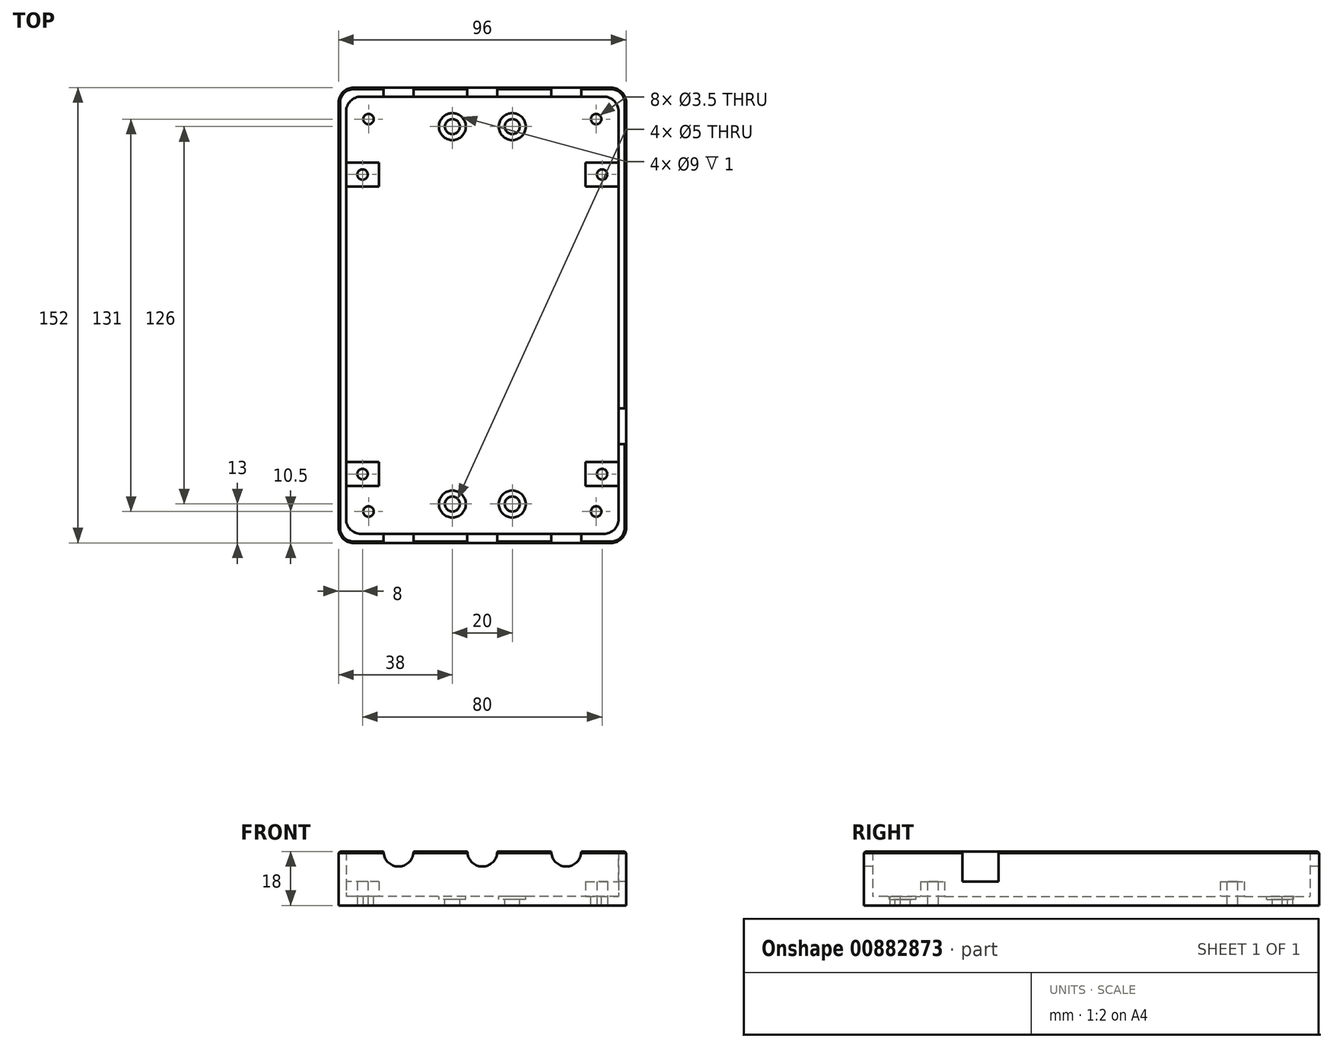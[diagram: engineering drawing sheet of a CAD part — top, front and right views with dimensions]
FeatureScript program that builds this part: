
annotation { "Feature Type Name" : "Feature", "Feature Type Description" : "" }
export const myFeature = defineFeature(function(context is Context, id is Id, definition is map)
    precondition{}
    {
        {
            var Q0;
            Q0=qCreatedBy(makeId("Top.planeOp"),FACE);
            var sketch = newSketch(context, id + "F0", { "sketchPlane" : qUnion([Q0])});
            skLineSegment(sketch, "E0.bottom", {"start": v(48, -76) * mm, "end": v(-48, -76) * mm});
            skLineSegment(sketch, "E0.top", {"start": v(48, 76) * mm, "end": v(-48, 76) * mm});
            skLineSegment(sketch, "E0.left", {"start": v(48, -76) * mm, "end": v(48, 76) * mm});
            skLineSegment(sketch, "E0.right", {"start": v(-48, -76) * mm, "end": v(-48, 76) * mm});
            skPoint(sketch, "E0.middle", {"position": v(0, 0) * mm});
            skSolve(sketch);
        }
        {
            var Q0;
            Q0 = qSketchRegion(id + "F0", true);
            extrude(context, id + "F1", {"entities" : qUnion([Q0]), "depth" : 3 * mm, "offsetDistance" : 25 * mm});
        }
        {
            var Q0;
            Q0=makeQuery(id+"F1.opExtrude","CAP_FACE",FACE,{"disambiguationData":[OSD([sQuery(id+"F0.wireOp",EDGE,"E0.bottom"),sQuery(id+"F0.wireOp",EDGE,"E0.top"),sQuery(id+"F0.wireOp",EDGE,"E0.left"),sQuery(id+"F0.wireOp",EDGE,"E0.right")])],"isStart":false});
            var sketch = newSketch(context, id + "F2", { "sketchPlane" : qUnion([Q0])});
            skLineSegment(sketch, "E1.bottom", {"start": v(48, -76) * mm, "end": v(-48, -76) * mm});
            skLineSegment(sketch, "E1.top", {"start": v(48, 76) * mm, "end": v(-48, 76) * mm});
            skLineSegment(sketch, "E1.left", {"start": v(48, -76) * mm, "end": v(48, 76) * mm});
            skLineSegment(sketch, "E1.right", {"start": v(-48, -76) * mm, "end": v(-48, 76) * mm});
            skPoint(sketch, "E1.middle", {"position": v(0, 0) * mm});
            skLineSegment(sketch, "E2.bottom", {"start": v(45.5, -73) * mm, "end": v(-45.5, -73) * mm});
            skLineSegment(sketch, "E2.top", {"start": v(45.5, 73) * mm, "end": v(-45.5, 73) * mm});
            skLineSegment(sketch, "E2.left", {"start": v(45.5, -73) * mm, "end": v(45.5, 73) * mm});
            skLineSegment(sketch, "E2.right", {"start": v(-45.5, -73) * mm, "end": v(-45.5, 73) * mm});
            skSolve(sketch);
        }
        {
            var Q0;
            Q0 = qSketchRegion(id + "F2", true);
            extrude(context, id + "F3", {"entities" : qUnion([Q0]), "operationType" : NewBodyOperationType.ADD, "depth" : 15 * mm, "offsetDistance" : 25 * mm});
        }
        {
            var Q0;
            Q0=makeQuery(id+"F1.opExtrude","CAP_FACE",FACE,{"disambiguationData":[OSD([sQuery(id+"F0.wireOp",EDGE,"E0.bottom"),sQuery(id+"F0.wireOp",EDGE,"E0.top"),sQuery(id+"F0.wireOp",EDGE,"E0.left"),sQuery(id+"F0.wireOp",EDGE,"E0.right")])],"isStart":false});
            var sketch = newSketch(context, id + "F4", { "sketchPlane" : qUnion([Q0])});
            skCircle(sketch, "E3", {"center": v(-38, 65.5) * mm, "radius": 1.75 * mm});
            skCircle(sketch, "E4.MirrorC", {"center": v(38, 65.5) * mm, "radius": 1.75 * mm});
            skCircle(sketch, "E5.MirrorC", {"center": v(-38, -65.5) * mm, "radius": 1.75 * mm});
            skCircle(sketch, "E6.MirrorC", {"center": v(38, -65.5) * mm, "radius": 1.75 * mm});
            skSolve(sketch);
        }
        {
            var Q0;
            Q0 = qSketchRegion(id + "F4", true);
            extrude(context, id + "F5", {"entities" : qUnion([Q0]), "operationType" : NewBodyOperationType.REMOVE, "endBound" : BoundingType.UP_TO_NEXT, "oppositeDirection" : true, "depth" : 25 * mm, "offsetDistance" : 25 * mm});
        }
        {
            var Q0;
            Q0=makeQuery(id+"F3.boolean.opBoolean","MERGE",EDGE,{"derivedFrom":[makeQuery(id+"F1.opExtrude","SWEPT_EDGE",EDGE,{"disambiguationData":[OSD([sQuery(id+"F0.wireOp",EDGE,"E0.bottom"),sQuery(id+"F0.wireOp",EDGE,"E0.right")])]}),makeQuery(id+"F3.opExtrude","SWEPT_EDGE",EDGE,{"disambiguationData":[OSD([sQuery(id+"F2.wireOp",EDGE,"E1.bottom"),sQuery(id+"F2.wireOp",EDGE,"E1.right")])]})]});
            var Q1;
            Q1=makeQuery(id+"F3.boolean.opBoolean","MERGE",EDGE,{"derivedFrom":[makeQuery(id+"F1.opExtrude","SWEPT_EDGE",EDGE,{"disambiguationData":[OSD([sQuery(id+"F0.wireOp",EDGE,"E0.bottom"),sQuery(id+"F0.wireOp",EDGE,"E0.left")])]}),makeQuery(id+"F3.opExtrude","SWEPT_EDGE",EDGE,{"disambiguationData":[OSD([sQuery(id+"F2.wireOp",EDGE,"E1.bottom"),sQuery(id+"F2.wireOp",EDGE,"E1.left")])]})]});
            var Q2;
            Q2=makeQuery(id+"F3.opExtrude","SWEPT_EDGE",EDGE,{"disambiguationData":[OSD([sQuery(id+"F2.wireOp",EDGE,"E2.bottom"),sQuery(id+"F2.wireOp",EDGE,"E2.left")])]});
            var Q3;
            Q3=makeQuery(id+"F3.opExtrude","SWEPT_EDGE",EDGE,{"disambiguationData":[OSD([sQuery(id+"F2.wireOp",EDGE,"E2.bottom"),sQuery(id+"F2.wireOp",EDGE,"E2.right")])]});
            var Q4;
            Q4=makeQuery(id+"F3.boolean.opBoolean","MERGE",EDGE,{"derivedFrom":[makeQuery(id+"F1.opExtrude","SWEPT_EDGE",EDGE,{"disambiguationData":[OSD([sQuery(id+"F0.wireOp",EDGE,"E0.top"),sQuery(id+"F0.wireOp",EDGE,"E0.right")])]}),makeQuery(id+"F3.opExtrude","SWEPT_EDGE",EDGE,{"disambiguationData":[OSD([sQuery(id+"F2.wireOp",EDGE,"E1.top"),sQuery(id+"F2.wireOp",EDGE,"E1.right")])]})]});
            var Q5;
            Q5=makeQuery(id+"F3.opExtrude","SWEPT_EDGE",EDGE,{"disambiguationData":[OSD([sQuery(id+"F2.wireOp",EDGE,"E2.top"),sQuery(id+"F2.wireOp",EDGE,"E2.right")])]});
            var Q6;
            Q6=makeQuery(id+"F3.boolean.opBoolean","MERGE",EDGE,{"derivedFrom":[makeQuery(id+"F1.opExtrude","SWEPT_EDGE",EDGE,{"disambiguationData":[OSD([sQuery(id+"F0.wireOp",EDGE,"E0.top"),sQuery(id+"F0.wireOp",EDGE,"E0.left")])]}),makeQuery(id+"F3.opExtrude","SWEPT_EDGE",EDGE,{"disambiguationData":[OSD([sQuery(id+"F2.wireOp",EDGE,"E1.top"),sQuery(id+"F2.wireOp",EDGE,"E1.left")])]})]});
            var Q7;
            Q7=makeQuery(id+"F3.opExtrude","SWEPT_EDGE",EDGE,{"disambiguationData":[OSD([sQuery(id+"F2.wireOp",EDGE,"E2.top"),sQuery(id+"F2.wireOp",EDGE,"E2.left")])]});
            fillet(context, id + "F6", {"entities" : qUnion([Q0, Q1, Q2, Q3, Q4, Q5, Q6, Q7]), "radius" : 5 * mm, "tangentPropagation" : true, "allowEdgeOverflow" : false});
        }
        {
            var Q0;
            Q0=makeQuery(id+"F3.boolean.opBoolean","MERGE",FACE,{"derivedFrom":[makeQuery(id+"F1.opExtrude","SWEPT_FACE",FACE,{"disambiguationData":[OSD([sQuery(id+"F0.wireOp",EDGE,"E0.bottom")])]}),makeQuery(id+"F3.opExtrude","SWEPT_FACE",FACE,{"disambiguationData":[OSD([sQuery(id+"F2.wireOp",EDGE,"E1.bottom")])]})]});
            var sketch = newSketch(context, id + "F7", { "sketchPlane" : qUnion([Q0])});
            skCircle(sketch, "E7", {"center": v(-28, 18) * mm, "radius": 5 * mm});
            skCircle(sketch, "E8", {"center": v(0, 18) * mm, "radius": 5 * mm});
            skCircle(sketch, "E9", {"center": v(28, 18) * mm, "radius": 5 * mm});
            skSolve(sketch);
        }
        {
            var Q0;
            Q0 = qSketchRegion(id + "F7", true);
            extrude(context, id + "F8", {"entities" : qUnion([Q0]), "operationType" : NewBodyOperationType.REMOVE, "endBound" : BoundingType.THROUGH_ALL, "oppositeDirection" : true, "depth" : 25 * mm, "offsetDistance" : 25 * mm});
        }
        {
            var Q0;
            Q0=makeQuery(id+"F1.opExtrude","CAP_FACE",FACE,{"disambiguationData":[OSD([sQuery(id+"F0.wireOp",EDGE,"E0.bottom"),sQuery(id+"F0.wireOp",EDGE,"E0.top"),sQuery(id+"F0.wireOp",EDGE,"E0.left"),sQuery(id+"F0.wireOp",EDGE,"E0.right")])],"isStart":false});
            var sketch = newSketch(context, id + "F9", { "sketchPlane" : qUnion([Q0])});
            skLineSegment(sketch, "E10.bottom", {"start": v(-34.5, -49) * mm, "end": v(-45.5, -49) * mm});
            skLineSegment(sketch, "E10.top", {"start": v(-34.5, -57) * mm, "end": v(-45.5, -57) * mm});
            skLineSegment(sketch, "E10.left", {"start": v(-34.5, -49) * mm, "end": v(-34.5, -57) * mm});
            skLineSegment(sketch, "E10.right", {"start": v(-45.5, -49) * mm, "end": v(-45.5, -57) * mm});
            skPoint(sketch, "E10.middle", {"position": v(-40, -53) * mm});
            skLineSegment(sketch, "E11.MirrorCS", {"start": v(34.5, -49) * mm, "end": v(34.5, -57) * mm});
            skLineSegment(sketch, "E12.MirrorCS", {"start": v(34.5, -49) * mm, "end": v(45.5, -49) * mm});
            skLineSegment(sketch, "E13.MirrorCS", {"start": v(45.5, -49) * mm, "end": v(45.5, -57) * mm});
            skLineSegment(sketch, "E14.MirrorCS", {"start": v(34.5, -57) * mm, "end": v(45.5, -57) * mm});
            skLineSegment(sketch, "E15.0.1.0", {"start": v(-34.5, 51) * mm, "end": v(-45.5, 51) * mm});
            skLineSegment(sketch, "E15.0.1.1", {"start": v(-34.5, 51) * mm, "end": v(-34.5, 43) * mm});
            skLineSegment(sketch, "E15.0.1.2", {"start": v(-34.5, 43) * mm, "end": v(-45.5, 43) * mm});
            skLineSegment(sketch, "E15.0.1.3", {"start": v(-45.5, 51) * mm, "end": v(-45.5, 43) * mm});
            skLineSegment(sketch, "E15.0.1.4", {"start": v(34.5, 51) * mm, "end": v(34.5, 43) * mm});
            skLineSegment(sketch, "E15.0.1.5", {"start": v(34.5, 51) * mm, "end": v(45.5, 51) * mm});
            skLineSegment(sketch, "E15.0.1.6", {"start": v(34.5, 43) * mm, "end": v(45.5, 43) * mm});
            skLineSegment(sketch, "E15.0.1.7", {"start": v(45.5, 51) * mm, "end": v(45.5, 43) * mm});
            skLineSegment(sketch, "E15.direction1", {"start": v(-45.5, -49) * mm, "end": v(-20.5, -49) * mm, "construction": true});
            skLineSegment(sketch, "E15.direction2", {"start": v(-45.5, -49) * mm, "end": v(-45.5, 51) * mm, "construction": true});
            skSolve(sketch);
        }
        {
            var Q0;
            Q0 = qSketchRegion(id + "F9", true);
            extrude(context, id + "F10", {"entities" : qUnion([Q0]), "operationType" : NewBodyOperationType.ADD, "depth" : 5 * mm, "offsetDistance" : 25 * mm});
        }
        {
            var Q0;
            Q0=makeQuery(id+"F1.opExtrude","CAP_FACE",FACE,{"disambiguationData":[OSD([sQuery(id+"F0.wireOp",EDGE,"E0.bottom"),sQuery(id+"F0.wireOp",EDGE,"E0.top"),sQuery(id+"F0.wireOp",EDGE,"E0.left"),sQuery(id+"F0.wireOp",EDGE,"E0.right")])],"isStart":false});
            var sketch = newSketch(context, id + "F11", { "sketchPlane" : qUnion([Q0])});
            skCircle(sketch, "E16", {"center": v(-40, -53) * mm, "radius": 1.75 * mm});
            skCircle(sketch, "E17.MirrorC", {"center": v(40, -53) * mm, "radius": 1.75 * mm});
            skCircle(sketch, "E18.0.1.0", {"center": v(-40, 47) * mm, "radius": 1.75 * mm});
            skCircle(sketch, "E18.0.1.1", {"center": v(40, 47) * mm, "radius": 1.75 * mm});
            skLineSegment(sketch, "E18.direction1", {"start": v(-40, -53) * mm, "end": v(-15, -53) * mm, "construction": true});
            skLineSegment(sketch, "E18.direction2", {"start": v(-40, -53) * mm, "end": v(-40, 47) * mm, "construction": true});
            skSolve(sketch);
        }
        {
            var Q0;
            Q0 = qSketchRegion(id + "F11", true);
            extrude(context, id + "F12", {"entities" : qUnion([Q0]), "operationType" : NewBodyOperationType.REMOVE, "endBound" : BoundingType.THROUGH_ALL, "depth" : 25 * mm, "offsetDistance" : 25 * mm});
        }
        {
            var Q0;
            Q0 = qSketchRegion(id + "F11", true);
            extrude(context, id + "F13", {"entities" : qUnion([Q0]), "operationType" : NewBodyOperationType.REMOVE, "oppositeDirection" : true, "depth" : 25 * mm, "offsetDistance" : 25 * mm});
        }
        {
            var Q0;
            Q0=makeQuery(id+"F1.opExtrude","CAP_FACE",FACE,{"disambiguationData":[OSD([sQuery(id+"F0.wireOp",EDGE,"E0.bottom"),sQuery(id+"F0.wireOp",EDGE,"E0.top"),sQuery(id+"F0.wireOp",EDGE,"E0.left"),sQuery(id+"F0.wireOp",EDGE,"E0.right")])],"isStart":false});
            var sketch = newSketch(context, id + "F14", { "sketchPlane" : qUnion([Q0])});
            skCircle(sketch, "E19", {"center": v(-10, -63) * mm, "radius": 2.5 * mm});
            skCircle(sketch, "E20.MirrorC", {"center": v(10, -63) * mm, "radius": 2.5 * mm});
            skCircle(sketch, "E21.MirrorC", {"center": v(-10, 63) * mm, "radius": 2.5 * mm});
            skCircle(sketch, "E22.MirrorC", {"center": v(10, 63) * mm, "radius": 2.5 * mm});
            skSolve(sketch);
        }
        {
            var Q0;
            Q0 = qSketchRegion(id + "F14", true);
            extrude(context, id + "F15", {"entities" : qUnion([Q0]), "operationType" : NewBodyOperationType.REMOVE, "endBound" : BoundingType.THROUGH_ALL, "oppositeDirection" : true, "depth" : 25 * mm, "offsetDistance" : 25 * mm});
        }
        {
            var Q0;
            Q0=makeQuery(id+"F3.opExtrude","SWEPT_FACE",FACE,{"disambiguationData":[OSD([sQuery(id+"F2.wireOp",EDGE,"E2.left")])]});
            var sketch = newSketch(context, id + "F16", { "sketchPlane" : qUnion([Q0])});
            skLineSegment(sketch, "E23.bottom", {"start": v(43, 8) * mm, "end": v(31, 8) * mm});
            skLineSegment(sketch, "E23.top", {"start": v(43, 28.9) * mm, "end": v(31, 28.9) * mm});
            skLineSegment(sketch, "E23.left", {"start": v(43, 8) * mm, "end": v(43, 28.9) * mm});
            skLineSegment(sketch, "E23.right", {"start": v(31, 8) * mm, "end": v(31, 28.9) * mm});
            skLineSegment(sketch, "E24", {"start": v(49, 8) * mm, "end": v(27.36, 8) * mm, "construction": true});
            skSolve(sketch);
        }
        {
            var Q0;
            Q0 = qSketchRegion(id + "F16", true);
            extrude(context, id + "F17", {"entities" : qUnion([Q0]), "operationType" : NewBodyOperationType.REMOVE, "endBound" : BoundingType.THROUGH_ALL, "oppositeDirection" : true, "depth" : 25 * mm, "offsetDistance" : 25 * mm});
        }
        {
            var Q0;
            {var subQ0=sQuery(id+"F2.wireOp",EDGE,"E1.left");Q0=makeQuery(id+"F17.boolean.opBoolean","SPLIT",EDGE,{"disambiguationData":[TD([makeQuery(id+"F17.opExtrude","SWEPT_FACE",FACE,{"disambiguationData":[OSD([sQuery(id+"F16.wireOp",EDGE,"E23.right")])]})])],"derivedFrom":makeQuery(id+"F3.opExtrude","CAP_EDGE",EDGE,{"disambiguationData":[OSD([subQ0])],"isStart":false})});}
            var Q1;
            {var subQ0=sQuery(id+"F2.wireOp",EDGE,"E1.left");Q1=makeQuery(id+"F17.boolean.opBoolean","SPLIT",EDGE,{"disambiguationData":[TD([makeQuery(id+"F17.opExtrude","SWEPT_FACE",FACE,{"disambiguationData":[OSD([sQuery(id+"F16.wireOp",EDGE,"E23.left")])]})])],"derivedFrom":makeQuery(id+"F3.opExtrude","CAP_EDGE",EDGE,{"disambiguationData":[OSD([subQ0])],"isStart":false})});}
            var Q2;
            {var subQ0=sQuery(id+"F2.wireOp",EDGE,"E1.left");var subQ1=sQuery(id+"F2.wireOp",EDGE,"E1.bottom");Q2=makeQuery(id+"F6.opFillet","BLEND_EDGE",EDGE,{"blendedFrom":[makeQuery(id+"F3.boolean.opBoolean","MERGE",EDGE,{"derivedFrom":[makeQuery(id+"F1.opExtrude","SWEPT_EDGE",EDGE,{"disambiguationData":[OSD([sQuery(id+"F0.wireOp",EDGE,"E0.bottom"),sQuery(id+"F0.wireOp",EDGE,"E0.left")])]}),makeQuery(id+"F3.opExtrude","SWEPT_EDGE",EDGE,{"disambiguationData":[OSD([subQ1,subQ0])]})]}),makeQuery(id+"F3.opExtrude","CAP_FACE",FACE,{"disambiguationData":[OSD([subQ1,sQuery(id+"F2.wireOp",EDGE,"E1.top"),subQ0,sQuery(id+"F2.wireOp",EDGE,"E1.right"),sQuery(id+"F2.wireOp",EDGE,"E2.bottom"),sQuery(id+"F2.wireOp",EDGE,"E2.top"),sQuery(id+"F2.wireOp",EDGE,"E2.left"),sQuery(id+"F2.wireOp",EDGE,"E2.right")])],"isStart":false})],"blendedInto":[makeQuery(id+"F3.opExtrude","CAP_FACE",FACE,{"disambiguationData":[OSD([subQ1,sQuery(id+"F2.wireOp",EDGE,"E1.top"),subQ0,sQuery(id+"F2.wireOp",EDGE,"E1.right"),sQuery(id+"F2.wireOp",EDGE,"E2.bottom"),sQuery(id+"F2.wireOp",EDGE,"E2.top"),sQuery(id+"F2.wireOp",EDGE,"E2.left"),sQuery(id+"F2.wireOp",EDGE,"E2.right")])],"isStart":false})]});}
            var Q3;
            {var subQ0=sQuery(id+"F2.wireOp",EDGE,"E1.bottom");Q3=makeQuery(id+"F8.boolean.opBoolean","SPLIT",EDGE,{"disambiguationData":[TD([makeQuery(id+"F1.opExtrude","SWEPT_FACE",FACE,{"disambiguationData":[OSD([sQuery(id+"F0.wireOp",EDGE,"E0.bottom")])]}),makeQuery(id+"F3.opExtrude","SWEPT_FACE",FACE,{"disambiguationData":[OSD([subQ0])]}),makeQuery(id+"F3.opExtrude","CAP_FACE",FACE,{"disambiguationData":[OSD([subQ0,sQuery(id+"F2.wireOp",EDGE,"E1.top"),sQuery(id+"F2.wireOp",EDGE,"E1.left"),sQuery(id+"F2.wireOp",EDGE,"E1.right"),sQuery(id+"F2.wireOp",EDGE,"E2.bottom"),sQuery(id+"F2.wireOp",EDGE,"E2.top"),sQuery(id+"F2.wireOp",EDGE,"E2.left"),sQuery(id+"F2.wireOp",EDGE,"E2.right")])],"isStart":false}),makeQuery(id+"F8.opExtrude","SWEPT_FACE",FACE,{"disambiguationData":[OSD([sQuery(id+"F7.wireOp",EDGE,"E8")])]}),makeQuery(id+"F8.opExtrude","SWEPT_FACE",FACE,{"disambiguationData":[OSD([sQuery(id+"F7.wireOp",EDGE,"E9")])]})])],"derivedFrom":makeQuery(id+"F3.opExtrude","CAP_EDGE",EDGE,{"disambiguationData":[OSD([subQ0])],"isStart":false})});}
            var Q4;
            {var subQ0=sQuery(id+"F2.wireOp",EDGE,"E1.bottom");Q4=makeQuery(id+"F8.boolean.opBoolean","SPLIT",EDGE,{"disambiguationData":[TD([makeQuery(id+"F1.opExtrude","SWEPT_FACE",FACE,{"disambiguationData":[OSD([sQuery(id+"F0.wireOp",EDGE,"E0.bottom")])]}),makeQuery(id+"F3.opExtrude","SWEPT_FACE",FACE,{"disambiguationData":[OSD([subQ0])]}),makeQuery(id+"F3.opExtrude","CAP_FACE",FACE,{"disambiguationData":[OSD([subQ0,sQuery(id+"F2.wireOp",EDGE,"E1.top"),sQuery(id+"F2.wireOp",EDGE,"E1.left"),sQuery(id+"F2.wireOp",EDGE,"E1.right"),sQuery(id+"F2.wireOp",EDGE,"E2.bottom"),sQuery(id+"F2.wireOp",EDGE,"E2.top"),sQuery(id+"F2.wireOp",EDGE,"E2.left"),sQuery(id+"F2.wireOp",EDGE,"E2.right")])],"isStart":false}),makeQuery(id+"F8.opExtrude","SWEPT_FACE",FACE,{"disambiguationData":[OSD([sQuery(id+"F7.wireOp",EDGE,"E7")])]}),makeQuery(id+"F8.opExtrude","SWEPT_FACE",FACE,{"disambiguationData":[OSD([sQuery(id+"F7.wireOp",EDGE,"E8")])]})])],"derivedFrom":makeQuery(id+"F3.opExtrude","CAP_EDGE",EDGE,{"disambiguationData":[OSD([subQ0])],"isStart":false})});}
            var Q5;
            {var subQ0=sQuery(id+"F2.wireOp",EDGE,"E1.right");var subQ1=sQuery(id+"F2.wireOp",EDGE,"E1.bottom");var subQ2=sQuery(id+"F0.wireOp",EDGE,"E0.bottom");Q5=makeQuery(id+"F8.boolean.opBoolean","SPLIT",EDGE,{"disambiguationData":[TD([makeQuery(id+"F1.opExtrude","SWEPT_FACE",FACE,{"disambiguationData":[OSD([subQ2])]}),makeQuery(id+"F3.opExtrude","SWEPT_FACE",FACE,{"disambiguationData":[OSD([subQ1])]}),makeQuery(id+"F3.opExtrude","CAP_FACE",FACE,{"disambiguationData":[OSD([subQ1,sQuery(id+"F2.wireOp",EDGE,"E1.top"),sQuery(id+"F2.wireOp",EDGE,"E1.left"),subQ0,sQuery(id+"F2.wireOp",EDGE,"E2.bottom"),sQuery(id+"F2.wireOp",EDGE,"E2.top"),sQuery(id+"F2.wireOp",EDGE,"E2.left"),sQuery(id+"F2.wireOp",EDGE,"E2.right")])],"isStart":false}),makeQuery(id+"F6.opFillet","BLEND_FACE",FACE,{"disambiguationData":[OSD([subQ2,sQuery(id+"F0.wireOp",EDGE,"E0.right"),subQ1,subQ0])]}),makeQuery(id+"F8.opExtrude","SWEPT_FACE",FACE,{"disambiguationData":[OSD([sQuery(id+"F7.wireOp",EDGE,"E7")])]})])],"derivedFrom":makeQuery(id+"F3.opExtrude","CAP_EDGE",EDGE,{"disambiguationData":[OSD([subQ1])],"isStart":false})});}
            var Q6;
            {var subQ0=sQuery(id+"F2.wireOp",EDGE,"E1.top");Q6=makeQuery(id+"F8.boolean.opBoolean","SPLIT",EDGE,{"disambiguationData":[TD([makeQuery(id+"F1.opExtrude","SWEPT_FACE",FACE,{"disambiguationData":[OSD([sQuery(id+"F0.wireOp",EDGE,"E0.top")])]}),makeQuery(id+"F3.opExtrude","CAP_FACE",FACE,{"disambiguationData":[OSD([sQuery(id+"F2.wireOp",EDGE,"E1.bottom"),subQ0,sQuery(id+"F2.wireOp",EDGE,"E1.left"),sQuery(id+"F2.wireOp",EDGE,"E1.right"),sQuery(id+"F2.wireOp",EDGE,"E2.bottom"),sQuery(id+"F2.wireOp",EDGE,"E2.top"),sQuery(id+"F2.wireOp",EDGE,"E2.left"),sQuery(id+"F2.wireOp",EDGE,"E2.right")])],"isStart":false}),makeQuery(id+"F3.opExtrude","SWEPT_FACE",FACE,{"disambiguationData":[OSD([subQ0])]}),makeQuery(id+"F8.opExtrude","SWEPT_FACE",FACE,{"disambiguationData":[OSD([sQuery(id+"F7.wireOp",EDGE,"E7")])]}),makeQuery(id+"F8.opExtrude","SWEPT_FACE",FACE,{"disambiguationData":[OSD([sQuery(id+"F7.wireOp",EDGE,"E8")])]})])],"derivedFrom":makeQuery(id+"F3.opExtrude","CAP_EDGE",EDGE,{"disambiguationData":[OSD([subQ0])],"isStart":false})});}
            var Q7;
            {var subQ0=sQuery(id+"F2.wireOp",EDGE,"E1.top");Q7=makeQuery(id+"F8.boolean.opBoolean","SPLIT",EDGE,{"disambiguationData":[TD([makeQuery(id+"F1.opExtrude","SWEPT_FACE",FACE,{"disambiguationData":[OSD([sQuery(id+"F0.wireOp",EDGE,"E0.top")])]}),makeQuery(id+"F3.opExtrude","CAP_FACE",FACE,{"disambiguationData":[OSD([sQuery(id+"F2.wireOp",EDGE,"E1.bottom"),subQ0,sQuery(id+"F2.wireOp",EDGE,"E1.left"),sQuery(id+"F2.wireOp",EDGE,"E1.right"),sQuery(id+"F2.wireOp",EDGE,"E2.bottom"),sQuery(id+"F2.wireOp",EDGE,"E2.top"),sQuery(id+"F2.wireOp",EDGE,"E2.left"),sQuery(id+"F2.wireOp",EDGE,"E2.right")])],"isStart":false}),makeQuery(id+"F3.opExtrude","SWEPT_FACE",FACE,{"disambiguationData":[OSD([subQ0])]}),makeQuery(id+"F8.opExtrude","SWEPT_FACE",FACE,{"disambiguationData":[OSD([sQuery(id+"F7.wireOp",EDGE,"E8")])]}),makeQuery(id+"F8.opExtrude","SWEPT_FACE",FACE,{"disambiguationData":[OSD([sQuery(id+"F7.wireOp",EDGE,"E9")])]})])],"derivedFrom":makeQuery(id+"F3.opExtrude","CAP_EDGE",EDGE,{"disambiguationData":[OSD([subQ0])],"isStart":false})});}
            chamfer(context, id + "F18", {"entities" : qUnion([Q0, Q1, Q2, Q3, Q4, Q5, Q6, Q7]), "width" : .5 * mm, "tangentPropagation" : true});
        }
        {
            var Q0;
            Q0=makeQuery(id+"F1.opExtrude","CAP_FACE",FACE,{"disambiguationData":[OSD([sQuery(id+"F0.wireOp",EDGE,"E0.bottom"),sQuery(id+"F0.wireOp",EDGE,"E0.top"),sQuery(id+"F0.wireOp",EDGE,"E0.left"),sQuery(id+"F0.wireOp",EDGE,"E0.right")])],"isStart":false});
            var sketch = newSketch(context, id + "F19", { "sketchPlane" : qUnion([Q0])});
            skCircle(sketch, "E25", {"center": v(10, 63) * mm, "radius": 4.5 * mm});
            skCircle(sketch, "E26.MirrorC", {"center": v(-10, 63) * mm, "radius": 4.5 * mm});
            skCircle(sketch, "E27.MirrorC", {"center": v(10, -63) * mm, "radius": 4.5 * mm});
            skCircle(sketch, "E28.MirrorC", {"center": v(-10, -63) * mm, "radius": 4.5 * mm});
            skSolve(sketch);
        }
        {
            var Q0;
            Q0 = qSketchRegion(id + "F19", true);
            extrude(context, id + "F20", {"entities" : qUnion([Q0]), "operationType" : NewBodyOperationType.REMOVE, "oppositeDirection" : true, "depth" : 1 * mm, "offsetDistance" : 25 * mm});
        }
    });
